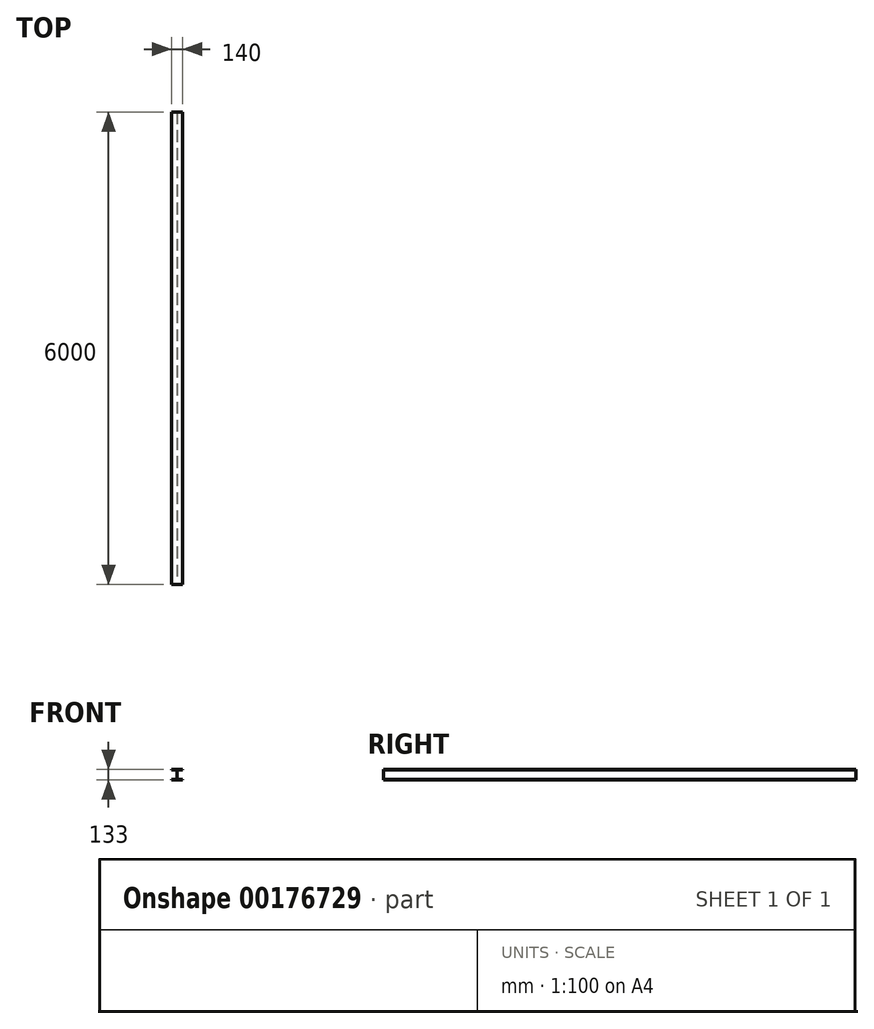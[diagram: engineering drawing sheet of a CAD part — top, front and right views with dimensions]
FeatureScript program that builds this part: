
annotation { "Feature Type Name" : "Feature", "Feature Type Description" : "" }
export const myFeature = defineFeature(function(context is Context, id is Id, definition is map)
    precondition{}
    {
        {
            var Q0;
            Q0=qCreatedBy(makeId("Front.planeOp"),FACE);
            var sketch = newSketch(context, id + "F0", { "sketchPlane" : qUnion([Q0])});
            skLineSegment(sketch, "E0", {"start": v(-70, -66.5) * mm, "end": v(70, -66.5) * mm});
            skLineSegment(sketch, "E1", {"start": v(70, -66.5) * mm, "end": v(70, -58) * mm});
            skLineSegment(sketch, "E2", {"start": v(70, -58) * mm, "end": v(2.75, -58) * mm});
            skLineSegment(sketch, "E3", {"start": v(2.75, -58) * mm, "end": v(2.75, 58) * mm});
            skLineSegment(sketch, "E4", {"start": v(2.75, 58) * mm, "end": v(70, 58) * mm});
            skLineSegment(sketch, "E5", {"start": v(70, 58) * mm, "end": v(70, 66.5) * mm});
            skLineSegment(sketch, "E6", {"start": v(70, 66.5) * mm, "end": v(-70, 66.5) * mm});
            skLineSegment(sketch, "E7", {"start": v(-70, 66.5) * mm, "end": v(-70, 58) * mm});
            skLineSegment(sketch, "E8", {"start": v(-70, 58) * mm, "end": v(-2.75, 58) * mm});
            skLineSegment(sketch, "E9", {"start": v(-2.75, 58) * mm, "end": v(-2.75, -58) * mm});
            skLineSegment(sketch, "E10", {"start": v(-2.75, -58) * mm, "end": v(-70, -58) * mm});
            skLineSegment(sketch, "E11", {"start": v(-70, -58) * mm, "end": v(-70, -66.5) * mm});
            skSolve(sketch);
        }
        {
            var Q0;
            Q0=sQuery(id+"F0.wireOp",EDGE,"E0");
            var Q1;
            Q1=sQuery(id+"F0.wireOp",EDGE,"E1");
            var Q2;
            Q2=sQuery(id+"F0.wireOp",EDGE,"E2");
            var Q3;
            Q3=sQuery(id+"F0.wireOp",EDGE,"E3");
            var Q4;
            Q4=sQuery(id+"F0.wireOp",EDGE,"E4");
            var Q5;
            Q5=sQuery(id+"F0.wireOp",EDGE,"E5");
            var Q6;
            Q6=sQuery(id+"F0.wireOp",EDGE,"E6");
            var Q7;
            Q7=sQuery(id+"F0.wireOp",EDGE,"E7");
            var Q8;
            Q8=sQuery(id+"F0.wireOp",EDGE,"E8");
            var Q9;
            Q9=sQuery(id+"F0.wireOp",EDGE,"E9");
            var Q10;
            Q10=sQuery(id+"F0.wireOp",EDGE,"E10");
            var Q11;
            Q11=sQuery(id+"F0.wireOp",EDGE,"E11");
            extrude(context, id + "F1", {"bodyType" : ToolBodyType.SURFACE, "surfaceEntities" : qUnion([Q0, Q1, Q2, Q3, Q4, Q5, Q6, Q7, Q8, Q9, Q10, Q11]), "depth" : 6000 * mm});
        }
    });
